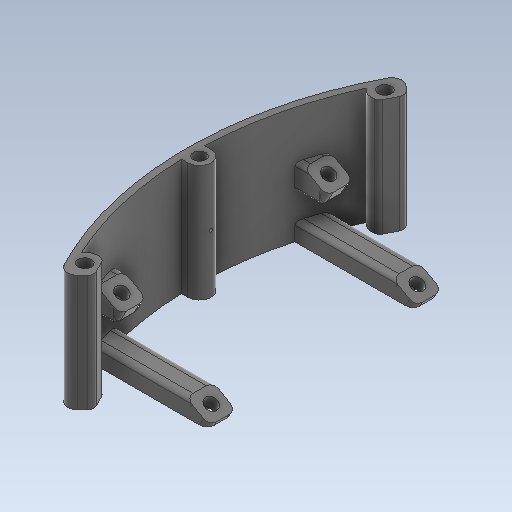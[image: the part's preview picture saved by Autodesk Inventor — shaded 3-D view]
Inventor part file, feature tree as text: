
AUTODESK INVENTOR PART (.ipt)
format: ipt  version: 2020 (Build 240168000, 168)  size: 1,423,360 bytes
history: native  units: mm
features: projected_geometry x32, extrude x20, sketch x13, other x9, fillet x1
ambient origin geometry x8: Origin, YZ Plane, XZ Plane, XY Plane, X Axis, Y Axis, Z Axis, Center Point
bodies: Body1 (feature_tree)
feature tree (75):
  other  "Твердое тело1"
  extrude  "outer"  TaperAngle=45.0deg  [1 undecoded]
  extrude  "inner"  Depth=7.0mm
  sketch  "Эскиз3"
  extrude  "Выдавливание3"  Depth=20.0mm
  extrude  "Выдавливание4"  Depth=7.0mm
  sketch  "Эскиз4"
  extrude  "Выдавливание5"  Depth=3.2mm
  extrude  "Выдавливание6"  Depth=59.0mm
  sketch  "Эскиз5"
  extrude  "Выдавливание7"  Depth=83.0mm
  extrude  "Выдавливание8"  Depth=69.0mm
  sketch  "Эскиз6"
  extrude  "Выдавливание9"  Depth=55.0mm
  extrude  "Выдавливание10"  Depth=3.0mm
  fillet  "Сопряжение1"  Radius=8.0mm
  other  "РабПлоскость2"
  other  "РабПлоскость3"
  sketch  "Эскиз10"
  sketch  "Эскиз11"
  other  "РабПлоскость4"
  other  "РабПлоскость5"
  other  "РабОсь2"
  other  "РабОсь1"
  sketch  "Эскиз12"
  extrude  "Выдавливание12"  Depth=5.0mm
  sketch  "Эскиз8"
  extrude  "asterisk"  Depth=2.0mm
  other  "РабПлоскость7"
  sketch  "Эскиз13"
  extrude  "Выдавливание13"  Depth=40.0mm TaperAngle=360.0deg
  extrude  "Выдавливание14"  Depth=2.0mm
  extrude  "Выдавливание15"  Depth=105.0mm
  extrude  "Выдавливание17"  Depth=2.0mm
  extrude  "Выдавливание18"  Depth=2.0mm TaperAngle=0.0deg
  extrude  "Выдавливание16"  Depth=3.5mm
  extrude  "Выдавливание19"  Depth=2.0mm
  extrude  "Выдавливание20"  Depth=6.0mm
  sketch  "Эскиз1"
  sketch  "Эскиз2"
  projected_geometry  "Спроецированная петля1"
  projected_geometry  "Спроецированная петля2"
  projected_geometry  "Спроецированная петля3"
  projected_geometry  "Спроецированная петля4"
  projected_geometry  "Спроецированная петля5"
  projected_geometry  "Спроецированная петля8"
  projected_geometry  "Спроецированная петля9"
  projected_geometry  "Спроецированная петля10"
  projected_geometry  "Спроецированная петля11"
  projected_geometry  "Спроецированная петля12"
  other  "РабПлоскость6"
  projected_geometry  "Спроецированная петля13"
  projected_geometry  "Спроецированная петля14"
  projected_geometry  "Спроецированная петля15"
  projected_geometry  "Спроецированная петля16"
  projected_geometry  "Спроецированная петля17"
  projected_geometry  "Спроецированная петля18"
  projected_geometry  "Спроецированная петля19"
  projected_geometry  "Спроецированная петля20"
  projected_geometry  "Спроецированная петля21"
  projected_geometry  "Спроецированная петля22"
  projected_geometry  "Спроецированная петля23"
  projected_geometry  "Спроецированная петля24"
  projected_geometry  "Спроецированная петля25"
  projected_geometry  "Спроецированная петля26"
  projected_geometry  "Спроецированная петля27"
  projected_geometry  "Спроецированная петля28"
  projected_geometry  "Спроецированная петля29"
  projected_geometry  "Спроецированная петля30"
  projected_geometry  "Спроецированная петля31"
  projected_geometry  "Спроецированная петля32"
  sketch  "Эскиз14"
  projected_geometry  "Спроецированная петля33"
  sketch  "Эскиз15"
  projected_geometry  "Спроецированная петля34"
note: 1 required parameter value undecoded (feature->parameter linkage not recoverable at this tier; creation-order binding heuristic only, values carry confidence <= 0.55)
